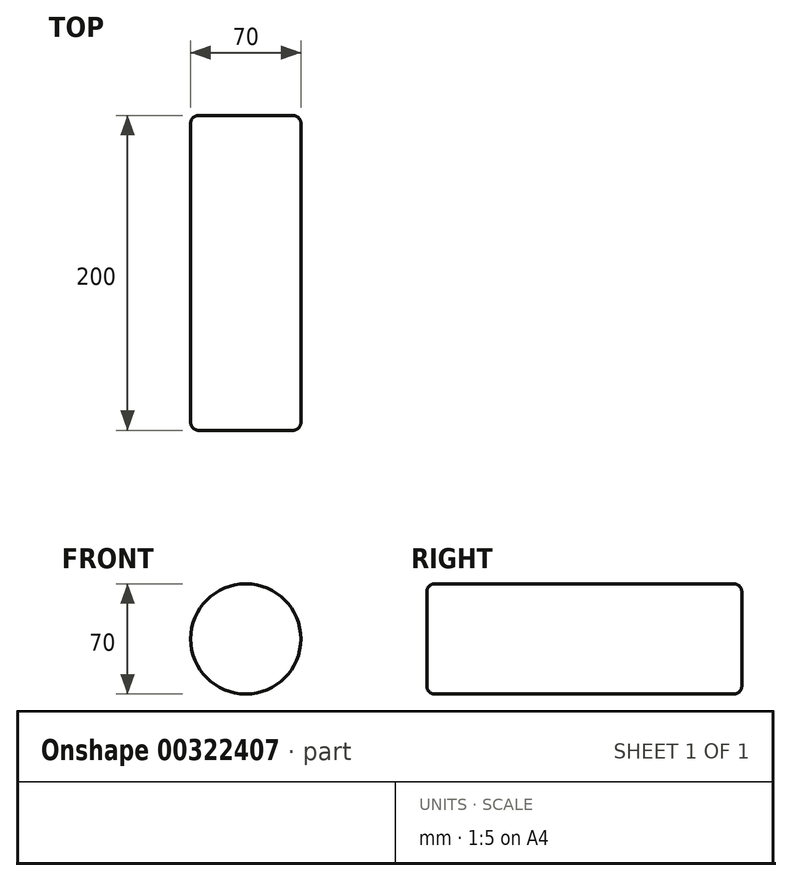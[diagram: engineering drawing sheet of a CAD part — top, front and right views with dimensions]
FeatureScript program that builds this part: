
annotation { "Feature Type Name" : "Feature", "Feature Type Description" : "" }
export const myFeature = defineFeature(function(context is Context, id is Id, definition is map)
    precondition{}
    {
        {
            var Q0;
            Q0=qCreatedBy(makeId("Front.planeOp"),FACE);
            var sketch = newSketch(context, id + "F0", { "sketchPlane" : qUnion([Q0])});
            skCircle(sketch, "E0", {"center": v(0, 0) * mm, "radius": 35 * mm});
            skSolve(sketch);
        }
        {
            var Q0;
            Q0=makeQuery(id+"F0.imprint","IMPRINT",FACE,{"disambiguationData":[TD([[makeQuery(id+"F0.imprint","IMPRINT",EDGE,{"derivedFrom":sQuery(id+"F0.wireOp",EDGE,"E0")}),1.0]])]});
            extrude(context, id + "F1", {"entities" : qUnion([Q0]), "depth" : 100 * mm, "hasSecondDirection" : true, "secondDirectionOppositeDirection" : true, "secondDirectionDepth" : 100 * mm});
        }
        {
            var Q0;
            Q0=makeQuery(id+"F1.opExtrude","CAP_EDGE",EDGE,{"disambiguationData":[OSD([sQuery(id+"F0.wireOp",EDGE,"E0")])],"isStart":false});
            var Q1;
            Q1=makeQuery(id+"F1.opExtrude","CAP_EDGE",EDGE,{"disambiguationData":[OSD([sQuery(id+"F0.wireOp",EDGE,"E0")])],"isStart":true});
            fillet(context, id + "F2", {"entities" : qUnion([Q0, Q1]), "radius" : 5 * mm, "tangentPropagation" : true, "allowEdgeOverflow" : false});
        }
    });
